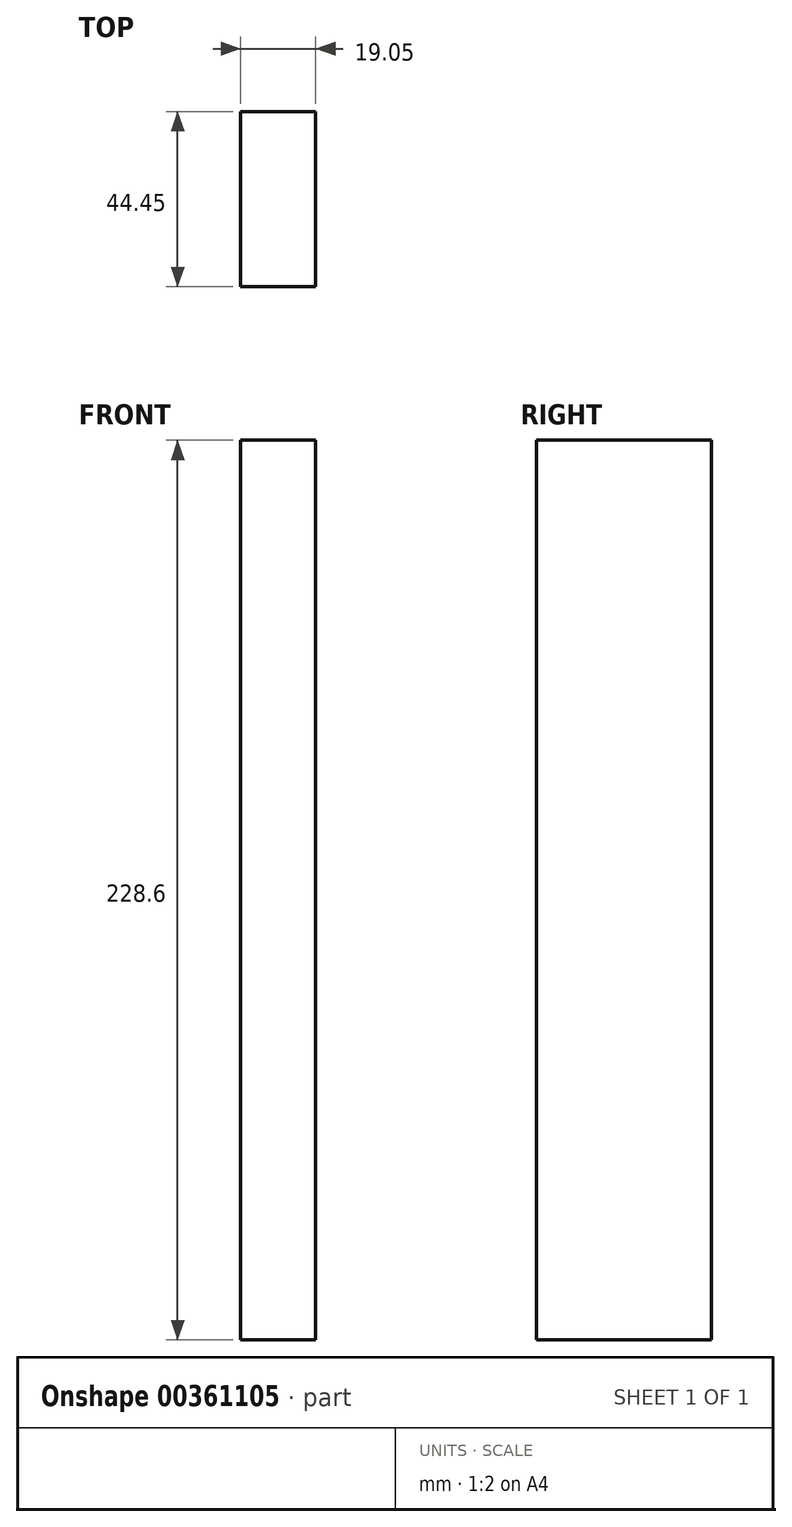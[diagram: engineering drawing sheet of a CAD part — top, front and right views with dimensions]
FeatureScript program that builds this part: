
annotation { "Feature Type Name" : "Feature", "Feature Type Description" : "" }
export const myFeature = defineFeature(function(context is Context, id is Id, definition is map)
    precondition{}
    {
        {
            var Q0;
            Q0=qCreatedBy(makeId("Right.planeOp"),FACE);
            var sketch = newSketch(context, id + "F0", { "sketchPlane" : qUnion([Q0])});
            skLineSegment(sketch, "E0.bottom", {"start": v(-115.08, 83.28) * mm, "end": v(-70.63, 83.28) * mm});
            skLineSegment(sketch, "E0.top", {"start": v(-115.08, -145.32) * mm, "end": v(-70.63, -145.32) * mm});
            skLineSegment(sketch, "E0.left", {"start": v(-115.08, 83.28) * mm, "end": v(-115.08, -145.32) * mm});
            skLineSegment(sketch, "E0.right", {"start": v(-70.63, 83.28) * mm, "end": v(-70.63, -145.32) * mm});
            skSolve(sketch);
        }
        {
            var Q0;
            Q0=qSketchRegion(id+"F0",true);
            extrude(context, id + "F1", {"entities" : qUnion([Q0]), "depth" : 19.05 * mm});
        }
    });
